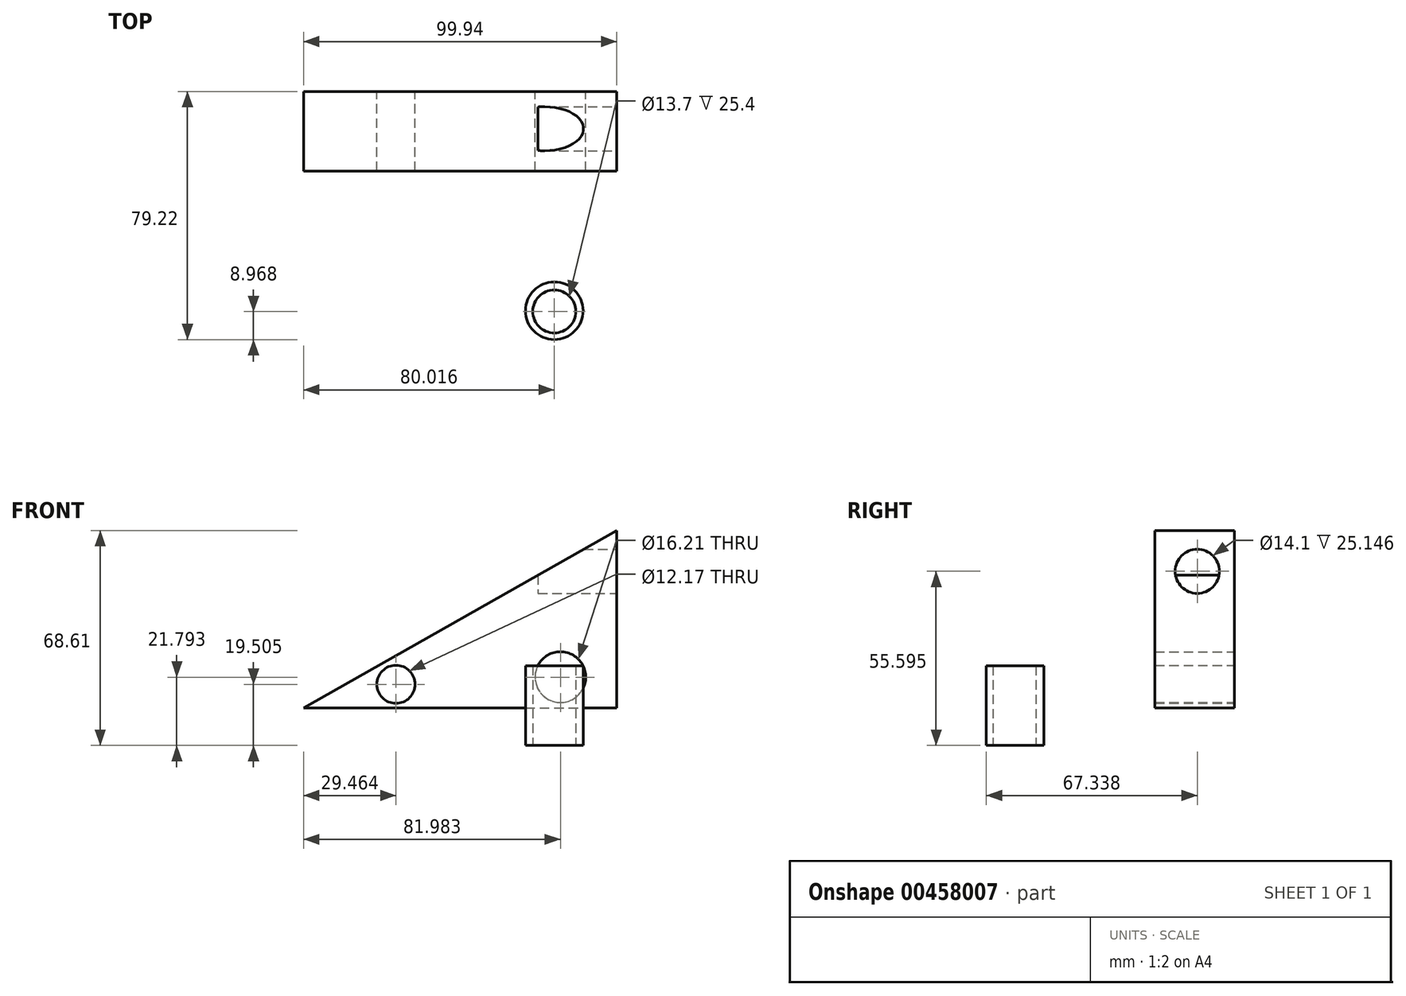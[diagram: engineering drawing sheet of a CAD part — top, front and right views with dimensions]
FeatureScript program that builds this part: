
annotation { "Feature Type Name" : "Feature", "Feature Type Description" : "" }
export const myFeature = defineFeature(function(context is Context, id is Id, definition is map)
    precondition{}
    {
        {
            var Q0;
            Q0=qCreatedBy(makeId("Front.planeOp"),FACE);
            var sketch = newSketch(context, id + "F0", { "sketchPlane" : qUnion([Q0])});
            skLineSegment(sketch, "E0", {"start": v(-63.84, 11.96) * mm, "end": v(36.1, 11.96) * mm});
            skLineSegment(sketch, "E1", {"start": v(-63.84, 11.96) * mm, "end": v(36.1, 68.61) * mm});
            skLineSegment(sketch, "E2", {"start": v(36.1, 68.61) * mm, "end": v(36.1, 11.96) * mm});
            skSolve(sketch);
        }
        {
            var Q0;
            Q0 = qSketchRegion(id + "F0", true);
            extrude(context, id + "F1", {"entities" : qUnion([Q0]), "depth" : 25.4 * mm});
        }
        {
            var Q0;
            Q0=qCreatedBy(makeId("Front.planeOp"),FACE);
            var sketch = newSketch(context, id + "F2", { "sketchPlane" : qUnion([Q0])});
            skCircle(sketch, "E3", {"center": v(18.14, 21.8) * mm, "radius": 8.1 * mm});
            skCircle(sketch, "E4", {"center": v(-34.38, 19.5) * mm, "radius": 6.09 * mm});
            skSolve(sketch);
        }
        {
            var Q0;
            Q0=makeQuery(id+"F2.imprint","IMPRINT",FACE,{"disambiguationData":[TD([[makeQuery(id+"F2.imprint","IMPRINT",EDGE,{"derivedFrom":sQuery(id+"F2.wireOp",EDGE,"E3")}),1.0]])]});
            extrude(context, id + "F3", {"entities" : qUnion([Q0]), "operationType" : NewBodyOperationType.REMOVE, "depth" : 50.8 * mm});
        }
        {
            var Q0;
            Q0=makeQuery(id+"F2.imprint","IMPRINT",FACE,{"disambiguationData":[TD([[makeQuery(id+"F2.imprint","IMPRINT",EDGE,{"derivedFrom":sQuery(id+"F2.wireOp",EDGE,"E4")}),1.0]])]});
            extrude(context, id + "F4", {"entities" : qUnion([Q0]), "operationType" : NewBodyOperationType.REMOVE, "depth" : 50.8 * mm});
        }
        {
            var Q0;
            Q0=makeQuery(id+"F1.opExtrude","SWEPT_FACE",FACE,{"disambiguationData":[OSD([sQuery(id+"F0.wireOp",EDGE,"E2")])]});
            var sketch = newSketch(context, id + "F5", { "sketchPlane" : qUnion([Q0])});
            skCircle(sketch, "E5", {"center": v(-11.88, 55.6) * mm, "radius": 7.05 * mm});
            skSolve(sketch);
        }
        {
            var Q0;
            Q0 = qSketchRegion(id + "F5", true);
            extrude(context, id + "F6", {"entities" : qUnion([Q0]), "operationType" : NewBodyOperationType.REMOVE, "oppositeDirection" : true, "depth" : 25.15 * mm});
        }
        {
            var Q0;
            Q0=qCreatedBy(makeId("Top.planeOp"),FACE);
            var sketch = newSketch(context, id + "F7", { "sketchPlane" : qUnion([Q0])});
            skCircle(sketch, "E6", {"center": v(16.18, -70.01) * mm, "radius": 9.2 * mm});
            skSolve(sketch);
        }
        {
            var Q0;
            Q0 = qSketchRegion(id + "F7", true);
            extrude(context, id + "F8", {"entities" : qUnion([Q0]), "depth" : 25.4 * mm});
        }
        {
            var Q0;
            Q0=qCreatedBy(makeId("Top.planeOp"),FACE);
            var sketch = newSketch(context, id + "F9", { "sketchPlane" : qUnion([Q0])});
            skCircle(sketch, "E7", {"center": v(16.18, -70.25) * mm, "radius": 6.85 * mm});
            skSolve(sketch);
        }
        {
            var Q0;
            Q0 = qSketchRegion(id + "F9", true);
            extrude(context, id + "F10", {"entities" : qUnion([Q0]), "operationType" : NewBodyOperationType.REMOVE, "depth" : 29.46 * mm});
        }
    });
